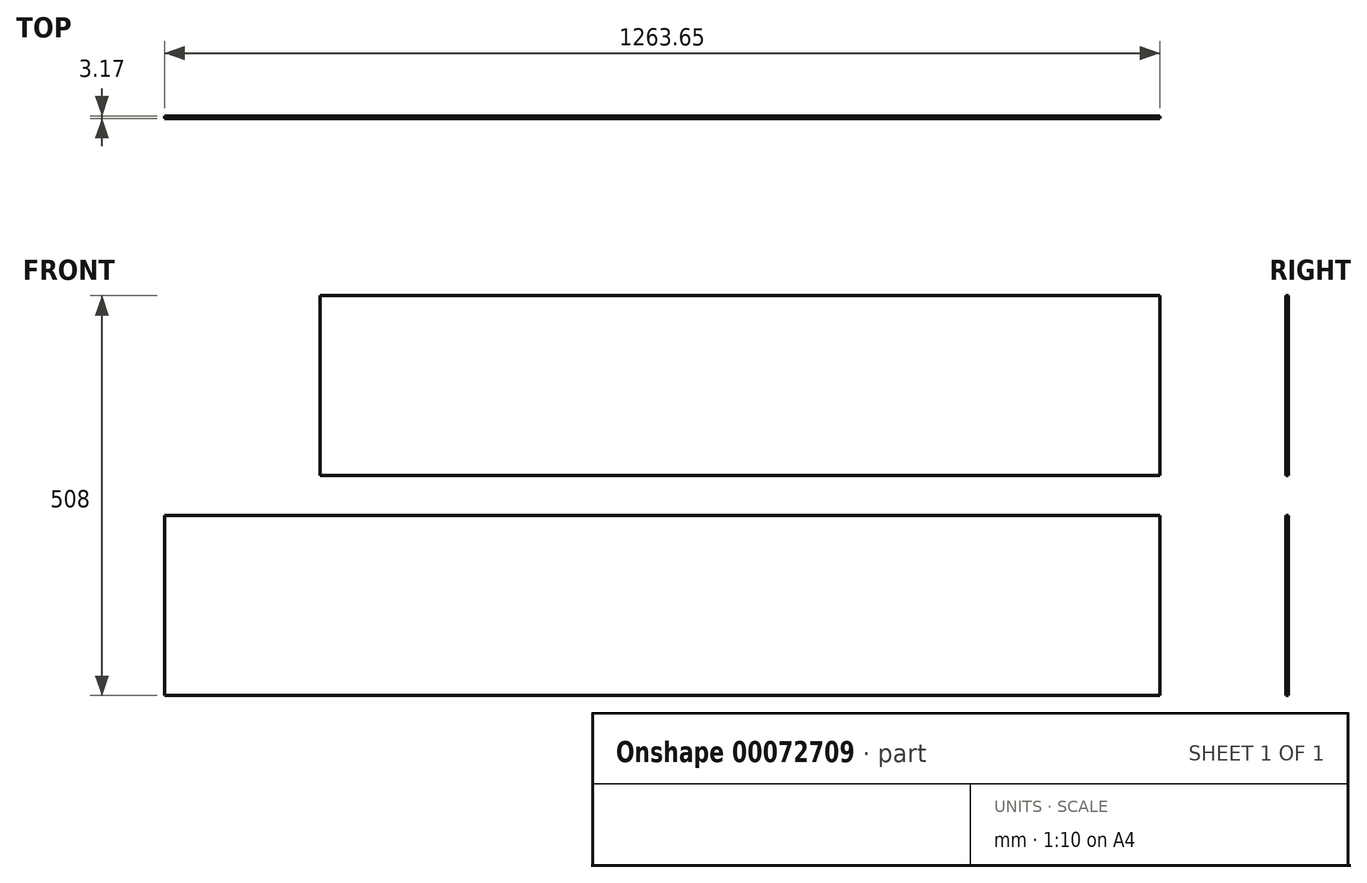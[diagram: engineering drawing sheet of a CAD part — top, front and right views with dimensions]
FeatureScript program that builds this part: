
annotation { "Feature Type Name" : "Feature", "Feature Type Description" : "" }
export const myFeature = defineFeature(function(context is Context, id is Id, definition is map)
    precondition{}
    {
        {
            var Q0;
            Q0=qCreatedBy(makeId("Front.planeOp"),FACE);
            var sketch = newSketch(context, id + "F0", { "sketchPlane" : qUnion([Q0])});
            skLineSegment(sketch, "E0.bottom", {"start": v(0, 0) * mm, "end": v(-1066.8, 0) * mm});
            skLineSegment(sketch, "E0.top", {"start": v(0, 228.6) * mm, "end": v(-1066.8, 228.6) * mm});
            skLineSegment(sketch, "E0.left", {"start": v(0, 0) * mm, "end": v(0, 228.6) * mm});
            skLineSegment(sketch, "E0.right", {"start": v(-1066.8, 0) * mm, "end": v(-1066.8, 228.6) * mm});
            skLineSegment(sketch, "E1.bottom", {"start": v(0, -50.8) * mm, "end": v(-1263.65, -50.8) * mm});
            skLineSegment(sketch, "E1.top", {"start": v(0, -279.4) * mm, "end": v(-1263.65, -279.4) * mm});
            skLineSegment(sketch, "E1.left", {"start": v(0, -50.8) * mm, "end": v(0, -279.4) * mm});
            skLineSegment(sketch, "E1.right", {"start": v(-1263.65, -50.8) * mm, "end": v(-1263.65, -279.4) * mm});
            skSolve(sketch);
        }
        {
            var Q0;
            Q0=makeQuery(id+"F0.imprint","IMPRINT",FACE,{"disambiguationData":[TD([[makeQuery(id+"F0.imprint","IMPRINT",EDGE,{"derivedFrom":sQuery(id+"F0.wireOp",EDGE,"E0.bottom")}),-1.0]])]});
            var Q1;
            Q1=makeQuery(id+"F0.imprint","IMPRINT",FACE,{"disambiguationData":[TD([[makeQuery(id+"F0.imprint","IMPRINT",EDGE,{"derivedFrom":sQuery(id+"F0.wireOp",EDGE,"E1.bottom")}),1.0]])]});
            extrude(context, id + "F1", {"entities" : qUnion([Q0, Q1]), "depth" : 3.17 * mm});
        }
    });
